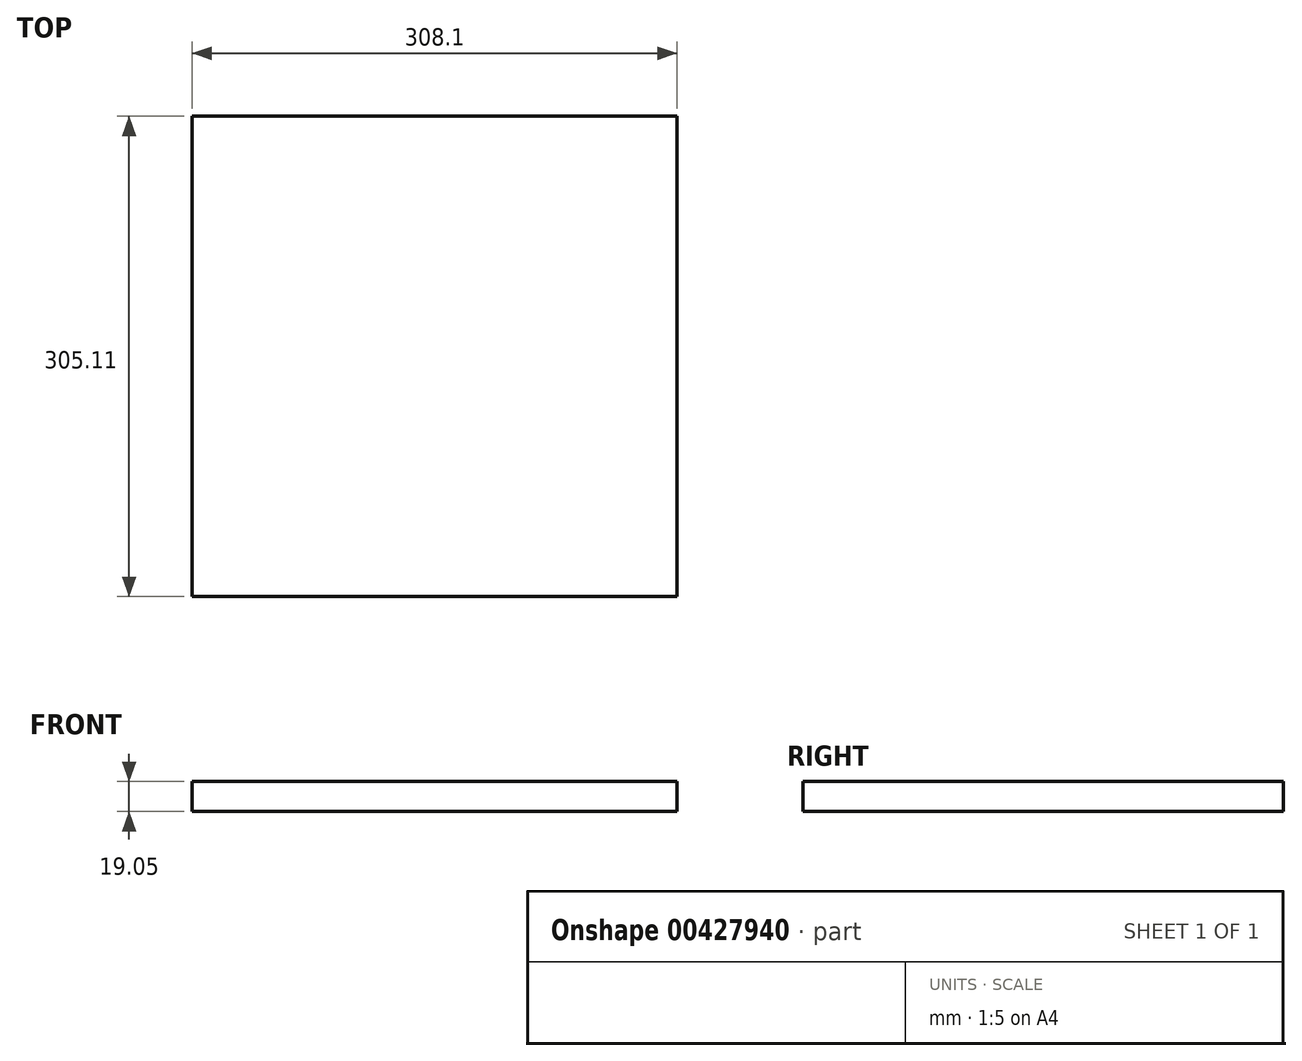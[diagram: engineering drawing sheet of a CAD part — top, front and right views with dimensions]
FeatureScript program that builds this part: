
annotation { "Feature Type Name" : "Feature", "Feature Type Description" : "" }
export const myFeature = defineFeature(function(context is Context, id is Id, definition is map)
    precondition{}
    {
        {
            var Q0;
            Q0=qCreatedBy(makeId("Top.planeOp"),FACE);
            var sketch = newSketch(context, id + "F0", { "sketchPlane" : qUnion([Q0])});
            skLineSegment(sketch, "E0.bottom", {"start": v(-75.11, 74.31) * mm, "end": v(232.99, 74.31) * mm});
            skLineSegment(sketch, "E0.top", {"start": v(-75.11, -230.8) * mm, "end": v(232.99, -230.8) * mm});
            skLineSegment(sketch, "E0.left", {"start": v(-75.11, 74.31) * mm, "end": v(-75.11, -230.8) * mm});
            skLineSegment(sketch, "E0.right", {"start": v(232.99, 74.31) * mm, "end": v(232.99, -230.8) * mm});
            skSolve(sketch);
        }
        {
            var Q0;
            Q0=makeQuery(id+"F0.imprint","IMPRINT",FACE,{"disambiguationData":[TD([[makeQuery(id+"F0.imprint","IMPRINT",EDGE,{"derivedFrom":sQuery(id+"F0.wireOp",EDGE,"E0.bottom")}),-1.0]])]});
            extrude(context, id + "F1", {"entities" : qUnion([Q0]), "depth" : 19.05 * mm});
        }
    });
